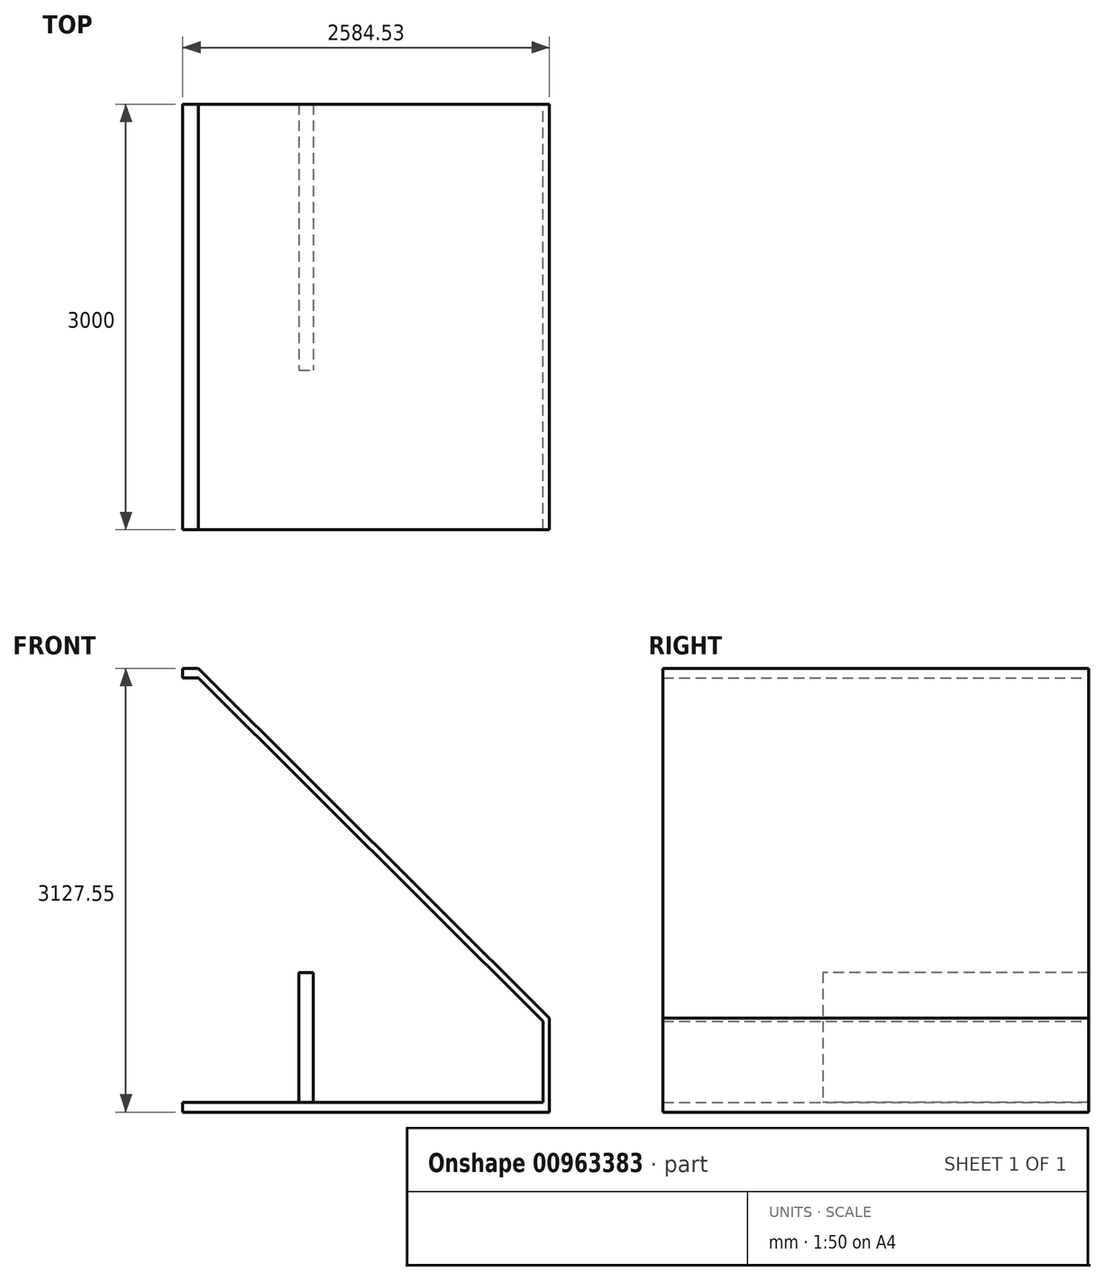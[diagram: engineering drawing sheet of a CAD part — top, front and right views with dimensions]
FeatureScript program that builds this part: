
annotation { "Feature Type Name" : "Feature", "Feature Type Description" : "" }
export const myFeature = defineFeature(function(context is Context, id is Id, definition is map)
    precondition{}
    {
        {
            var Q0;
            Q0=qCreatedBy(makeId("Front.planeOp"),FACE);
            var sketch = newSketch(context, id + "F0", { "sketchPlane" : qUnion([Q0])});
            skLineSegment(sketch, "E0", {"start": v(0, 0) * mm, "end": v(2540, 0) * mm});
            skLineSegment(sketch, "E1", {"start": v(0, 0) * mm, "end": v(0, 2990) * mm, "construction": true});
            skLineSegment(sketch, "E2", {"start": v(0, 2990) * mm, "end": v(110, 2990) * mm});
            skLineSegment(sketch, "E3", {"start": v(110, 2990) * mm, "end": v(2540, 570) * mm});
            skLineSegment(sketch, "E4", {"start": v(2540, 570) * mm, "end": v(2540, 0) * mm});
            skLineSegment(sketch, "E5", {"start": v(0, 2990) * mm, "end": v(0, 3058.44) * mm});
            skLineSegment(sketch, "E6", {"start": v(0, 3058.44) * mm, "end": v(110, 3058.44) * mm});
            skLineSegment(sketch, "E7", {"start": v(110, 3058.44) * mm, "end": v(2584.53, 594.1) * mm});
            skLineSegment(sketch, "E8", {"start": v(2584.53, 594.1) * mm, "end": v(2584.53, -69.1) * mm});
            skLineSegment(sketch, "E9", {"start": v(2584.53, -69.1) * mm, "end": v(0, -69.1) * mm});
            skLineSegment(sketch, "E10", {"start": v(0, -69.1) * mm, "end": v(0, 0) * mm});
            skSolve(sketch);
        }
        {
            var Q0;
            Q0=makeQuery(id+"F0.imprint","IMPRINT",FACE,{"disambiguationData":[TD([[makeQuery(id+"F0.imprint","IMPRINT",EDGE,{"derivedFrom":sQuery(id+"F0.wireOp",EDGE,"E0")}),-1.0]])]});
            extrude(context, id + "F1", {"entities" : qUnion([Q0]), "depth" : 3000 * mm, "offsetDistance" : 25 * mm});
        }
        {
            var Q0;
            Q0=makeQuery(id+"F1.opExtrude","SWEPT_FACE",FACE,{"disambiguationData":[OSD([sQuery(id+"F0.wireOp",EDGE,"E0")])]});
            var sketch = newSketch(context, id + "F2", { "sketchPlane" : qUnion([Q0])});
            skLineSegment(sketch, "E11.bottom", {"start": v(820, 0) * mm, "end": v(920, 0) * mm});
            skLineSegment(sketch, "E11.top", {"start": v(820, -1875) * mm, "end": v(920, -1875) * mm});
            skLineSegment(sketch, "E11.left", {"start": v(820, 0) * mm, "end": v(820, -1875) * mm});
            skLineSegment(sketch, "E11.right", {"start": v(920, 0) * mm, "end": v(920, -1875) * mm});
            skSolve(sketch);
        }
        {
            var Q0;
            Q0 = qSketchRegion(id + "F2", true);
            extrude(context, id + "F3", {"entities" : qUnion([Q0]), "operationType" : NewBodyOperationType.ADD, "depth" : 915 * mm, "offsetDistance" : 25 * mm});
        }
    });
